# Revit family: 3b56e8a4-c011-4e47-85b4-0de4efff14cf
name_source: partatom
category: Mechanical Equipment
revit_build: Autodesk Revit 2016 (Build: 20161004_0715(x64)
units: mm (PartAtom-declared; Revit-internal decimal feet)

## family parameters
Cut with Voids When Loaded = No
Host = Face
OmniClass Number = 23.75.70.21
OmniClass Title = Terminals for Air
Part Type = Normal
Room Calculation Point = No
Round Connector Dimension = Use Diameter
Shared = Yes

## types (1)
- 12" x 12"
    Default Elevation = 4' - 0"
    Depth = 0' - 0 5/8"
    Description = Ligature Resistant Exhaust/Supply Grille
    Finish = Metal-BSP-Powder Coat-White
    Height = 1' - 0"
    Insert Height = 0' - 8 7/8"
    Insert Width = 0' - 8 7/8"
    Manufacturer = Behavioral Safety Products
    Model = EG450
    Product Documentation Link = http://besafeprod.com
    Product Page URL = http://besafeprod.com
    Product data url = https://bimobject.com
    Type Image = <None>
    URL = http://besafeprod.com
    Width = 1' - 0"

## geometry (parser evidence)
native form markers: Blend x2, Sweep x3
no freeform markers — native parametric forms only
